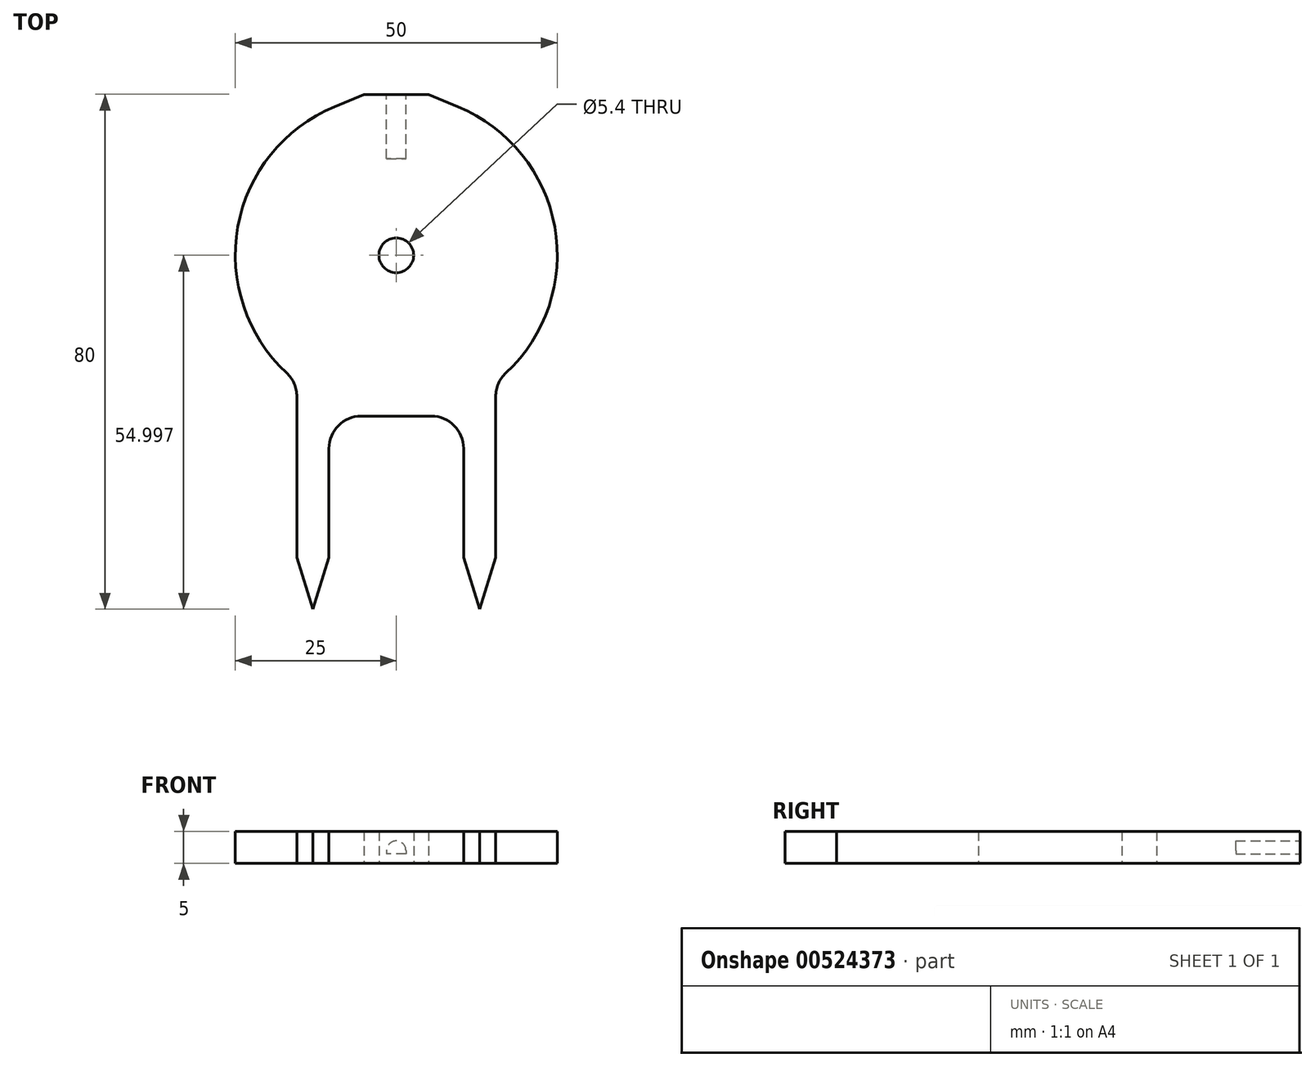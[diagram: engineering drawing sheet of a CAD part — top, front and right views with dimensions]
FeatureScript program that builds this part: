
annotation { "Feature Type Name" : "Feature", "Feature Type Description" : "" }
export const myFeature = defineFeature(function(context is Context, id is Id, definition is map)
    precondition{}
    {
        {
            var Q0;
            Q0=qCreatedBy(makeId("Top.planeOp"),FACE);
            var sketch = newSketch(context, id + "F0", { "sketchPlane" : qUnion([Q0])});
            skLineSegment(sketch, "E0.left", {"start": v(-15.45, 18.04) * mm, "end": v(-15.45, -7) * mm});
            skLineSegment(sketch, "E1.bottom", {"start": v(-5.45, 15) * mm, "end": v(0, 15) * mm});
            skLineSegment(sketch, "E2", {"start": v(-12.95, -15) * mm, "end": v(-10.45, -7) * mm});
            skLineSegment(sketch, "E3", {"start": v(-12.95, -15) * mm, "end": v(-15.45, -7) * mm});
            skArc(sketch, "E4", {"start": v(-9.62, 63.07) * mm, "mid": v(-24.6, 44.41) * mm, "end": v(-17.04, 21.7) * mm});
            skLineSegment(sketch, "E5", {"start": v(-10.45, -7) * mm, "end": v(-10.45, 10) * mm});
            skPoint(sketch, "E6.visualSharp", {"position": v(-10.45, 15) * mm});
            skArc(sketch, "E6.filletArc", {"start": v(-5.45, 15) * mm, "mid": v(-8.98, 13.53) * mm, "end": v(-10.45, 10) * mm});
            skPoint(sketch, "E7.visualSharp", {"position": v(-15.45, 20.34) * mm});
            skArc(sketch, "E7.filletArc", {"start": v(-15.45, 18.04) * mm, "mid": v(-15.86, 20.04) * mm, "end": v(-17.04, 21.7) * mm});
            skLineSegment(sketch, "E8", {"start": v(0, 65) * mm, "end": v(0, 15) * mm});
            skArc(sketch, "E9", {"start": v(0, 42.5) * mm, "mid": v(-2.5, 40) * mm, "end": v(0, 37.5) * mm});
            skLineSegment(sketch, "E10", {"start": v(0, 65) * mm, "end": v(-5, 65) * mm});
            skLineSegment(sketch, "E11", {"start": v(-5, 65) * mm, "end": v(-9.62, 63.07) * mm});
            skArc(sketch, "E12.MirrorCS", {"start": v(15.45, 18.04) * mm, "mid": v(15.86, 20.04) * mm, "end": v(17.04, 21.7) * mm});
            skLineSegment(sketch, "E13.MirrorCS", {"start": v(0, 65) * mm, "end": v(5, 65) * mm});
            skArc(sketch, "E14.MirrorCS", {"start": v(0, 42.5) * mm, "mid": v(2.5, 40) * mm, "end": v(0, 37.5) * mm});
            skLineSegment(sketch, "E15.MirrorCS", {"start": v(12.95, -15) * mm, "end": v(15.45, -7) * mm});
            skLineSegment(sketch, "E16.MirrorCS", {"start": v(5.45, 15) * mm, "end": v(0, 15) * mm});
            skPoint(sketch, "E17.MirrorP", {"position": v(15.45, 20.34) * mm});
            skArc(sketch, "E18.MirrorCS", {"start": v(9.62, 63.07) * mm, "mid": v(24.6, 44.41) * mm, "end": v(17.04, 21.7) * mm});
            skLineSegment(sketch, "E19.MirrorCS", {"start": v(5, 65) * mm, "end": v(9.62, 63.07) * mm});
            skArc(sketch, "E20.MirrorCS", {"start": v(5.45, 15) * mm, "mid": v(8.98, 13.53) * mm, "end": v(10.45, 10) * mm});
            skLineSegment(sketch, "E21.MirrorCS", {"start": v(10.45, -7) * mm, "end": v(10.45, 10) * mm});
            skLineSegment(sketch, "E22.MirrorCS", {"start": v(15.45, 18.04) * mm, "end": v(15.45, -7) * mm});
            skLineSegment(sketch, "E23.MirrorCS", {"start": v(12.95, -15) * mm, "end": v(10.45, -7) * mm});
            skPoint(sketch, "E24.MirrorP", {"position": v(10.45, 15) * mm});
            skSolve(sketch);
        }
        {
            var Q0;
            Q0=makeQuery(id+"F0.imprint","IMPRINT",FACE,{"disambiguationData":[TD([[makeQuery(id+"F0.imprint","IMPRINT",EDGE,{"derivedFrom":sQuery(id+"F0.wireOp",EDGE,"E0.left")}),1.0]])]});
            var Q1;
            {var subQ0=sQuery(id+"F0.wireOp",EDGE,"E9");Q1=makeQuery(id+"F0.imprint","IMPRINT",FACE,{"disambiguationData":[TD([[makeQuery(id+"F0.imprint","IMPRINT",EDGE,{"derivedFrom":subQ0}),1.0]])]});}
            var Q2;
            Q2=makeQuery(id+"F0.imprint","IMPRINT",FACE,{"disambiguationData":[TD([[makeQuery(id+"F0.imprint","IMPRINT",EDGE,{"derivedFrom":sQuery(id+"F0.wireOp",EDGE,"E12.MirrorCS")}),1.0]])]});
            var Q3;
            {var subQ0=sQuery(id+"F0.wireOp",EDGE,"E14.MirrorCS");Q3=makeQuery(id+"F0.imprint","IMPRINT",FACE,{"disambiguationData":[TD([[makeQuery(id+"F0.imprint","IMPRINT",EDGE,{"derivedFrom":subQ0}),-1.0]])]});}
            extrude(context, id + "F1", {"entities" : qUnion([Q0, Q1, Q2, Q3]), "depth" : 5 * mm, "offsetDistance" : 25 * mm});
        }
        {
            var Q0;
            Q0=sQuery(id+"F0.wireOp",VERTEX,"E4.center");
            var Q1;
            Q1=makeQuery(id+"F1.opExtrude","SWEPT_BODY",BODY,{"disambiguationData":[OSD([sQuery(id+"F0.wireOp",EDGE,"E0.left"),sQuery(id+"F0.wireOp",EDGE,"E1.bottom"),sQuery(id+"F0.wireOp",EDGE,"E2"),sQuery(id+"F0.wireOp",EDGE,"E3"),sQuery(id+"F0.wireOp",EDGE,"E4"),sQuery(id+"F0.wireOp",EDGE,"E5"),sQuery(id+"F0.wireOp",EDGE,"E6.filletArc"),sQuery(id+"F0.wireOp",EDGE,"E7.filletArc"),sQuery(id+"F0.wireOp",EDGE,"E10"),sQuery(id+"F0.wireOp",EDGE,"E11"),sQuery(id+"F0.wireOp",EDGE,"E12.MirrorCS"),sQuery(id+"F0.wireOp",EDGE,"E13.MirrorCS"),sQuery(id+"F0.wireOp",EDGE,"E15.MirrorCS"),sQuery(id+"F0.wireOp",EDGE,"E16.MirrorCS"),sQuery(id+"F0.wireOp",EDGE,"E18.MirrorCS"),sQuery(id+"F0.wireOp",EDGE,"E19.MirrorCS"),sQuery(id+"F0.wireOp",EDGE,"E20.MirrorCS"),sQuery(id+"F0.wireOp",EDGE,"E21.MirrorCS"),sQuery(id+"F0.wireOp",EDGE,"E22.MirrorCS"),sQuery(id+"F0.wireOp",EDGE,"E23.MirrorCS")])]});
            hole(context, id + "F2", {"style" : HoleStyle.SIMPLE, "endStyle" : HoleEndStyle.THROUGH, "oppositeDirection" : true, "holeDiameter" : 5.4 * mm, "isTappedThrough" : true, "tappedDepth" : 12 * mm, "tapClearance" : 3, "locations" : qUnion([Q0]), "scope" : qUnion([Q1])});
        }
        {
            var Q0;
            Q0=makeQuery(id+"F1.opExtrude","SWEPT_FACE",FACE,{"disambiguationData":[OSD([sQuery(id+"F0.wireOp",EDGE,"E10"),sQuery(id+"F0.wireOp",EDGE,"E13.MirrorCS")])]});
            var sketch = newSketch(context, id + "F3", { "sketchPlane" : qUnion([Q0])});
            skPoint(sketch, "E25", {"position": v(0, 2.5) * mm});
            skLineSegment(sketch, "E26.bottom", {"start": v(-1.5, 3.5) * mm, "end": v(1.5, 3.5) * mm});
            skLineSegment(sketch, "E26.top", {"start": v(-1.5, 1.5) * mm, "end": v(1.5, 1.5) * mm});
            skLineSegment(sketch, "E26.left", {"start": v(-1.5, 3.5) * mm, "end": v(-1.5, 1.5) * mm});
            skLineSegment(sketch, "E26.right", {"start": v(1.5, 3.5) * mm, "end": v(1.5, 1.5) * mm});
            skSolve(sketch);
        }
        {
            var Q0;
            Q0=makeQuery(id+"F3.imprint","IMPRINT",FACE,{"disambiguationData":[TD([[makeQuery(id+"F3.imprint","IMPRINT",EDGE,{"derivedFrom":sQuery(id+"F3.wireOp",EDGE,"E26.bottom")}),-1.0]])]});
            extrude(context, id + "F4", {"entities" : qUnion([Q0]), "operationType" : NewBodyOperationType.REMOVE, "oppositeDirection" : true, "depth" : 10 * mm, "offsetDistance" : 25 * mm});
        }
        {
            var Q0;
            Q0=makeQuery(id+"F4.boolean.opBoolean","COPY",EDGE,{"derivedFrom":makeQuery(id+"F4.opExtrude","SWEPT_EDGE",EDGE,{"disambiguationData":[OSD([sQuery(id+"F3.wireOp",EDGE,"E26.bottom"),sQuery(id+"F3.wireOp",EDGE,"E26.left")])]})});
            var Q1;
            Q1=makeQuery(id+"F4.boolean.opBoolean","COPY",EDGE,{"derivedFrom":makeQuery(id+"F4.opExtrude","SWEPT_EDGE",EDGE,{"disambiguationData":[OSD([sQuery(id+"F3.wireOp",EDGE,"E26.bottom"),sQuery(id+"F3.wireOp",EDGE,"E26.right")])]})});
            fillet(context, id + "F5", {"entities" : qUnion([Q0, Q1]), "radius" : 1.5 * mm, "tangentPropagation" : true, "allowEdgeOverflow" : false});
        }
    });
